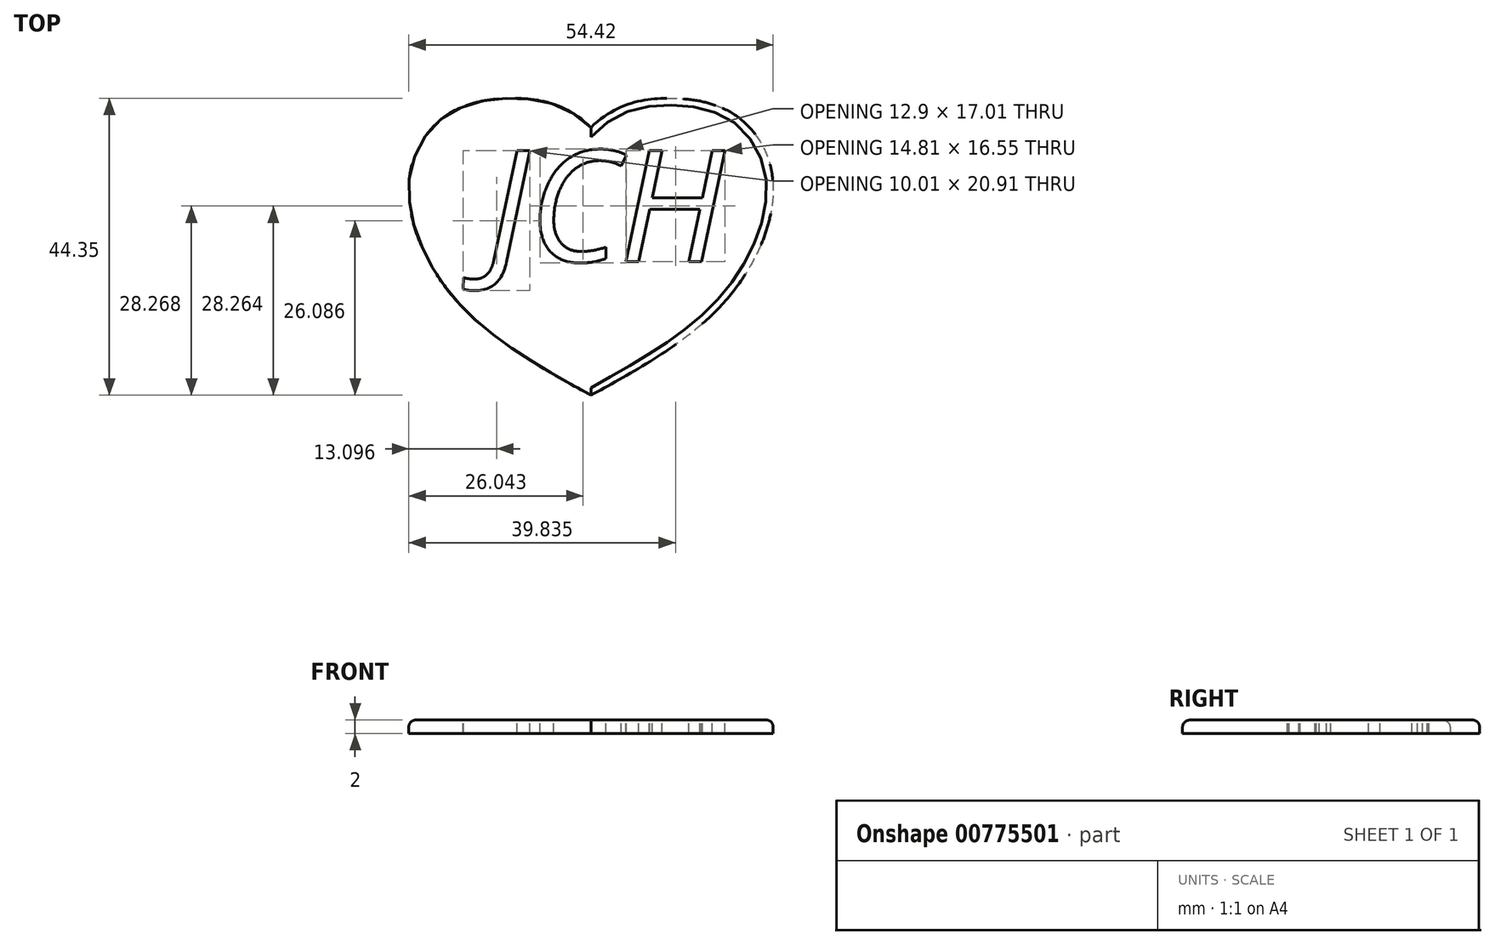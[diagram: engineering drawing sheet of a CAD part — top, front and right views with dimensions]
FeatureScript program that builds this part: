
annotation { "Feature Type Name" : "Feature", "Feature Type Description" : "" }
export const myFeature = defineFeature(function(context is Context, id is Id, definition is map)
    precondition{}
    {
        {
            var Q0;
            Q0=qCreatedBy(makeId("Top.planeOp"),FACE);
            var sketch = newSketch(context, id + "F0", { "sketchPlane" : qUnion([Q0])});
            skFitSpline(sketch, "E0", {"points": [v(0, 40) * mm, v(-12.4, 44.33) * mm, v(-18.67, 43.3) * mm, v(-23.19, 40.5) * mm, v(-26.76, 34.44) * mm, v(-26.76, 26.72) * mm, v(-24.3, 20.2) * mm, v(-19.7, 13.68) * mm, v(-11.24, 6.63) * mm, v(0, 0) * mm], "startDerivative": vector(-89.08, 87.77) * mm, "endDerivative": vector(67.58, -36.73) * mm});
            skLineSegment(sketch, "E1", {"start": v(0, 40) * mm, "end": v(0, 0) * mm});
            skSolve(sketch);
        }
        {
            var Q0;
            Q0=makeQuery(id+"F0.imprint","IMPRINT",FACE,{"disambiguationData":[TD([[makeQuery(id+"F0.imprint","IMPRINT",EDGE,{"derivedFrom":sQuery(id+"F0.wireOp",EDGE,"E0")}),1.0]])]});
            extrude(context, id + "F1", {"entities" : qUnion([Q0]), "depth" : 2 * mm, "offsetDistance" : 25 * mm});
        }
        {
            var Q0;
            Q0=makeQuery(id+"F1.opExtrude","SWEPT_BODY",BODY,{"disambiguationData":[OSD([sQuery(id+"F0.wireOp",EDGE,"E0"),sQuery(id+"F0.wireOp",EDGE,"E1")])]});
            var Q1;
            Q1=makeQuery(id+"F1.opExtrude","SWEPT_FACE",FACE,{"disambiguationData":[OSD([sQuery(id+"F0.wireOp",EDGE,"E1")])]});
            mirror(context, id + "F2", {"operationType" : NewBodyOperationType.ADD, "entities" : qUnion([Q0]), "mirrorPlane" : qUnion([Q1])});
        }
        {
            var Q0;
            {var subQ0=makeQuery(id+"F1.opExtrude","CAP_FACE",FACE,{"disambiguationData":[OSD([sQuery(id+"F0.wireOp",EDGE,"E0"),sQuery(id+"F0.wireOp",EDGE,"E1")])],"isStart":false});Q0=makeQuery(id+"F2.boolean.opBoolean","MERGE",FACE,{"derivedFrom":[subQ0,makeQuery(id+"F2.opPattern","COPY",FACE,{"derivedFrom":subQ0,"instanceName":"1"})]});}
            var sketch = newSketch(context, id + "F3", { "sketchPlane" : qUnion([Q0])});
            skText(sketch, "E2", { "text": " JCH", "fontName": "OpenSans-Italic.ttf"});
            const initialGuessF3  = {"E2": [-0.02153, 0.01999, 1, 0, 0.01669]};
            skSetInitialGuess(sketch, initialGuessF3);
            skSolve(sketch);
        }
        {
            var Q0;
            Q0=qSketchRegion(id+"F3",true);
            extrude(context, id + "F4", {"entities" : qUnion([Q0]), "operationType" : NewBodyOperationType.REMOVE, "oppositeDirection" : true, "depth" : 30 * mm, "offsetDistance" : 25 * mm});
        }
        {
            var Q0;
            Q0=makeQuery(id+"F2.opPattern","COPY",EDGE,{"derivedFrom":makeQuery(id+"F1.opExtrude","CAP_EDGE",EDGE,{"disambiguationData":[OSD([sQuery(id+"F0.wireOp",EDGE,"E0")])],"isStart":false}),"instanceName":"1"});
            var Q1;
            Q1=makeQuery(id+"F4.boolean.opBoolean","COPY",EDGE,{"derivedFrom":makeQuery(id+"F4.opExtrude","CAP_EDGE",EDGE,{"disambiguationData":[OSD([sQuery(id+"F3.wireOp",EDGE,"E2.sketch_text.stroke-37")])],"isStart":true})});
            var Q2;
            Q2=makeQuery(id+"F4.boolean.opBoolean","COPY",EDGE,{"derivedFrom":makeQuery(id+"F4.opExtrude","CAP_EDGE",EDGE,{"disambiguationData":[OSD([sQuery(id+"F3.wireOp",EDGE,"E2.sketch_text.stroke-3")])],"isStart":true})});
            var Q3;
            Q3=makeQuery(id+"F4.boolean.opBoolean","COPY",EDGE,{"derivedFrom":makeQuery(id+"F4.opExtrude","CAP_EDGE",EDGE,{"disambiguationData":[OSD([sQuery(id+"F3.wireOp",EDGE,"E2.sketch_text.stroke-54")])],"isStart":true})});
            var Q4;
            Q4=makeQuery(id+"F1.opExtrude","CAP_EDGE",EDGE,{"disambiguationData":[OSD([sQuery(id+"F0.wireOp",EDGE,"E0")])],"isStart":false});
            var Q5;
            Q5=makeQuery(id+"F4.boolean.opBoolean","COPY",EDGE,{"derivedFrom":makeQuery(id+"F4.opExtrude","CAP_EDGE",EDGE,{"disambiguationData":[OSD([sQuery(id+"F3.wireOp",EDGE,"E2.sketch_text.stroke-12")])],"isStart":true})});
            var Q6;
            Q6=makeQuery(id+"F4.boolean.opBoolean","COPY",EDGE,{"derivedFrom":makeQuery(id+"F4.opExtrude","CAP_EDGE",EDGE,{"disambiguationData":[OSD([sQuery(id+"F3.wireOp",EDGE,"E2.sketch_text.stroke-8")])],"isStart":true})});
            var Q7;
            Q7=makeQuery(id+"F4.boolean.opBoolean","COPY",EDGE,{"derivedFrom":makeQuery(id+"F4.opExtrude","CAP_EDGE",EDGE,{"disambiguationData":[OSD([sQuery(id+"F3.wireOp",EDGE,"E2.sketch_text.stroke-26")])],"isStart":true})});
            var Q8;
            Q8=makeQuery(id+"F4.boolean.opBoolean","COPY",EDGE,{"derivedFrom":makeQuery(id+"F4.opExtrude","CAP_EDGE",EDGE,{"disambiguationData":[OSD([sQuery(id+"F3.wireOp",EDGE,"E2.sketch_text.stroke-60")])],"isStart":true})});
            var Q9;
            Q9=makeQuery(id+"F4.boolean.opBoolean","COPY",EDGE,{"derivedFrom":makeQuery(id+"F4.opExtrude","CAP_EDGE",EDGE,{"disambiguationData":[OSD([sQuery(id+"F3.wireOp",EDGE,"E2.sketch_text.stroke-32")])],"isStart":true})});
            var Q10;
            Q10=makeQuery(id+"F4.boolean.opBoolean","COPY",EDGE,{"derivedFrom":makeQuery(id+"F4.opExtrude","CAP_EDGE",EDGE,{"disambiguationData":[OSD([sQuery(id+"F3.wireOp",EDGE,"E2.sketch_text.stroke-51")])],"isStart":true})});
            var Q11;
            Q11=makeQuery(id+"F4.boolean.opBoolean","COPY",EDGE,{"derivedFrom":makeQuery(id+"F4.opExtrude","CAP_EDGE",EDGE,{"disambiguationData":[OSD([sQuery(id+"F3.wireOp",EDGE,"E2.sketch_text.stroke-20")])],"isStart":true})});
            var Q12;
            Q12=makeQuery(id+"F4.boolean.opBoolean","COPY",EDGE,{"derivedFrom":makeQuery(id+"F4.opExtrude","CAP_EDGE",EDGE,{"disambiguationData":[OSD([sQuery(id+"F3.wireOp",EDGE,"E2.sketch_text.stroke-25")])],"isStart":true})});
            var Q13;
            Q13=makeQuery(id+"F4.boolean.opBoolean","COPY",EDGE,{"derivedFrom":makeQuery(id+"F4.opExtrude","CAP_EDGE",EDGE,{"disambiguationData":[OSD([sQuery(id+"F3.wireOp",EDGE,"E2.sketch_text.stroke-46")])],"isStart":true})});
            var Q14;
            Q14=makeQuery(id+"F4.boolean.opBoolean","COPY",EDGE,{"derivedFrom":makeQuery(id+"F4.opExtrude","CAP_EDGE",EDGE,{"disambiguationData":[OSD([sQuery(id+"F3.wireOp",EDGE,"E2.sketch_text.stroke-62")])],"isStart":true})});
            var Q15;
            Q15=makeQuery(id+"F4.boolean.opBoolean","COPY",EDGE,{"derivedFrom":makeQuery(id+"F4.opExtrude","CAP_EDGE",EDGE,{"disambiguationData":[OSD([sQuery(id+"F3.wireOp",EDGE,"E2.sketch_text.stroke-0")])],"isStart":true})});
            var Q16;
            Q16=makeQuery(id+"F4.boolean.opBoolean","COPY",EDGE,{"derivedFrom":makeQuery(id+"F4.opExtrude","CAP_EDGE",EDGE,{"disambiguationData":[OSD([sQuery(id+"F3.wireOp",EDGE,"E2.sketch_text.stroke-52")])],"isStart":true})});
            var Q17;
            Q17=makeQuery(id+"F4.boolean.opBoolean","COPY",EDGE,{"derivedFrom":makeQuery(id+"F4.opExtrude","CAP_EDGE",EDGE,{"disambiguationData":[OSD([sQuery(id+"F3.wireOp",EDGE,"E2.sketch_text.stroke-28")])],"isStart":true})});
            var Q18;
            Q18=makeQuery(id+"F4.boolean.opBoolean","COPY",EDGE,{"derivedFrom":makeQuery(id+"F4.opExtrude","CAP_EDGE",EDGE,{"disambiguationData":[OSD([sQuery(id+"F3.wireOp",EDGE,"E2.sketch_text.stroke-2")])],"isStart":true})});
            var Q19;
            Q19=makeQuery(id+"F4.boolean.opBoolean","COPY",EDGE,{"derivedFrom":makeQuery(id+"F4.opExtrude","CAP_EDGE",EDGE,{"disambiguationData":[OSD([sQuery(id+"F3.wireOp",EDGE,"E2.sketch_text.stroke-15")])],"isStart":true})});
            var Q20;
            Q20=makeQuery(id+"F4.boolean.opBoolean","COPY",EDGE,{"derivedFrom":makeQuery(id+"F4.opExtrude","CAP_EDGE",EDGE,{"disambiguationData":[OSD([sQuery(id+"F3.wireOp",EDGE,"E2.sketch_text.stroke-43")])],"isStart":true})});
            var Q21;
            Q21=makeQuery(id+"F4.boolean.opBoolean","COPY",EDGE,{"derivedFrom":makeQuery(id+"F4.opExtrude","CAP_EDGE",EDGE,{"disambiguationData":[OSD([sQuery(id+"F3.wireOp",EDGE,"E2.sketch_text.stroke-55")])],"isStart":true})});
            var Q22;
            Q22=makeQuery(id+"F4.boolean.opBoolean","COPY",EDGE,{"derivedFrom":makeQuery(id+"F4.opExtrude","CAP_EDGE",EDGE,{"disambiguationData":[OSD([sQuery(id+"F3.wireOp",EDGE,"E2.sketch_text.stroke-59")])],"isStart":true})});
            var Q23;
            Q23=makeQuery(id+"F4.boolean.opBoolean","COPY",EDGE,{"derivedFrom":makeQuery(id+"F4.opExtrude","CAP_EDGE",EDGE,{"disambiguationData":[OSD([sQuery(id+"F3.wireOp",EDGE,"E2.sketch_text.stroke-47")])],"isStart":true})});
            var Q24;
            Q24=makeQuery(id+"F4.boolean.opBoolean","COPY",EDGE,{"derivedFrom":makeQuery(id+"F4.opExtrude","CAP_EDGE",EDGE,{"disambiguationData":[OSD([sQuery(id+"F3.wireOp",EDGE,"E2.sketch_text.stroke-5")])],"isStart":true})});
            var Q25;
            Q25=makeQuery(id+"F4.boolean.opBoolean","COPY",EDGE,{"derivedFrom":makeQuery(id+"F4.opExtrude","CAP_EDGE",EDGE,{"disambiguationData":[OSD([sQuery(id+"F3.wireOp",EDGE,"E2.sketch_text.stroke-45")])],"isStart":true})});
            var Q26;
            Q26=makeQuery(id+"F4.boolean.opBoolean","COPY",EDGE,{"derivedFrom":makeQuery(id+"F4.opExtrude","CAP_EDGE",EDGE,{"disambiguationData":[OSD([sQuery(id+"F3.wireOp",EDGE,"E2.sketch_text.stroke-44")])],"isStart":true})});
            var Q27;
            Q27=makeQuery(id+"F4.boolean.opBoolean","COPY",EDGE,{"derivedFrom":makeQuery(id+"F4.opExtrude","CAP_EDGE",EDGE,{"disambiguationData":[OSD([sQuery(id+"F3.wireOp",EDGE,"E2.sketch_text.stroke-4")])],"isStart":true})});
            var Q28;
            Q28=makeQuery(id+"F4.boolean.opBoolean","COPY",EDGE,{"derivedFrom":makeQuery(id+"F4.opExtrude","CAP_EDGE",EDGE,{"disambiguationData":[OSD([sQuery(id+"F3.wireOp",EDGE,"E2.sketch_text.stroke-42")])],"isStart":true})});
            var Q29;
            Q29=makeQuery(id+"F4.boolean.opBoolean","COPY",EDGE,{"derivedFrom":makeQuery(id+"F4.opExtrude","CAP_EDGE",EDGE,{"disambiguationData":[OSD([sQuery(id+"F3.wireOp",EDGE,"E2.sketch_text.stroke-57")])],"isStart":true})});
            var Q30;
            Q30=makeQuery(id+"F4.boolean.opBoolean","COPY",EDGE,{"derivedFrom":makeQuery(id+"F4.opExtrude","CAP_EDGE",EDGE,{"disambiguationData":[OSD([sQuery(id+"F3.wireOp",EDGE,"E2.sketch_text.stroke-22")])],"isStart":true})});
            var Q31;
            Q31=makeQuery(id+"F4.boolean.opBoolean","COPY",EDGE,{"derivedFrom":makeQuery(id+"F4.opExtrude","CAP_EDGE",EDGE,{"disambiguationData":[OSD([sQuery(id+"F3.wireOp",EDGE,"E2.sketch_text.stroke-18")])],"isStart":true})});
            var Q32;
            Q32=makeQuery(id+"F4.boolean.opBoolean","COPY",EDGE,{"derivedFrom":makeQuery(id+"F4.opExtrude","CAP_EDGE",EDGE,{"disambiguationData":[OSD([sQuery(id+"F3.wireOp",EDGE,"E2.sketch_text.stroke-1")])],"isStart":true})});
            var Q33;
            Q33=makeQuery(id+"F4.boolean.opBoolean","COPY",EDGE,{"derivedFrom":makeQuery(id+"F4.opExtrude","CAP_EDGE",EDGE,{"disambiguationData":[OSD([sQuery(id+"F3.wireOp",EDGE,"E2.sketch_text.stroke-7")])],"isStart":true})});
            var Q34;
            Q34=makeQuery(id+"F4.boolean.opBoolean","COPY",EDGE,{"derivedFrom":makeQuery(id+"F4.opExtrude","CAP_EDGE",EDGE,{"disambiguationData":[OSD([sQuery(id+"F3.wireOp",EDGE,"E2.sketch_text.stroke-9")])],"isStart":true})});
            var Q35;
            Q35=makeQuery(id+"F4.boolean.opBoolean","COPY",EDGE,{"derivedFrom":makeQuery(id+"F4.opExtrude","CAP_EDGE",EDGE,{"disambiguationData":[OSD([sQuery(id+"F3.wireOp",EDGE,"E2.sketch_text.stroke-11")])],"isStart":true})});
            var Q36;
            Q36=makeQuery(id+"F4.boolean.opBoolean","COPY",EDGE,{"derivedFrom":makeQuery(id+"F4.opExtrude","CAP_EDGE",EDGE,{"disambiguationData":[OSD([sQuery(id+"F3.wireOp",EDGE,"E2.sketch_text.stroke-6")])],"isStart":true})});
            var Q37;
            Q37=makeQuery(id+"F4.boolean.opBoolean","COPY",EDGE,{"derivedFrom":makeQuery(id+"F4.opExtrude","CAP_EDGE",EDGE,{"disambiguationData":[OSD([sQuery(id+"F3.wireOp",EDGE,"E2.sketch_text.stroke-53")])],"isStart":true})});
            var Q38;
            Q38=makeQuery(id+"F4.boolean.opBoolean","COPY",EDGE,{"derivedFrom":makeQuery(id+"F4.opExtrude","CAP_EDGE",EDGE,{"disambiguationData":[OSD([sQuery(id+"F3.wireOp",EDGE,"E2.sketch_text.stroke-38")])],"isStart":true})});
            var Q39;
            Q39=makeQuery(id+"F4.boolean.opBoolean","COPY",EDGE,{"derivedFrom":makeQuery(id+"F4.opExtrude","CAP_EDGE",EDGE,{"disambiguationData":[OSD([sQuery(id+"F3.wireOp",EDGE,"E2.sketch_text.stroke-24")])],"isStart":true})});
            var Q40;
            Q40=makeQuery(id+"F4.boolean.opBoolean","COPY",EDGE,{"derivedFrom":makeQuery(id+"F4.opExtrude","CAP_EDGE",EDGE,{"disambiguationData":[OSD([sQuery(id+"F3.wireOp",EDGE,"E2.sketch_text.stroke-58")])],"isStart":true})});
            var Q41;
            Q41=makeQuery(id+"F4.boolean.opBoolean","COPY",EDGE,{"derivedFrom":makeQuery(id+"F4.opExtrude","CAP_EDGE",EDGE,{"disambiguationData":[OSD([sQuery(id+"F3.wireOp",EDGE,"E2.sketch_text.stroke-61")])],"isStart":true})});
            var Q42;
            Q42=makeQuery(id+"F4.boolean.opBoolean","COPY",EDGE,{"derivedFrom":makeQuery(id+"F4.opExtrude","CAP_EDGE",EDGE,{"disambiguationData":[OSD([sQuery(id+"F3.wireOp",EDGE,"E2.sketch_text.stroke-41")])],"isStart":true})});
            var Q43;
            Q43=makeQuery(id+"F4.boolean.opBoolean","COPY",EDGE,{"derivedFrom":makeQuery(id+"F4.opExtrude","CAP_EDGE",EDGE,{"disambiguationData":[OSD([sQuery(id+"F3.wireOp",EDGE,"E2.sketch_text.stroke-14")])],"isStart":true})});
            var Q44;
            Q44=makeQuery(id+"F4.boolean.opBoolean","COPY",EDGE,{"derivedFrom":makeQuery(id+"F4.opExtrude","CAP_EDGE",EDGE,{"disambiguationData":[OSD([sQuery(id+"F3.wireOp",EDGE,"E2.sketch_text.stroke-36")])],"isStart":true})});
            var Q45;
            Q45=makeQuery(id+"F4.boolean.opBoolean","COPY",EDGE,{"derivedFrom":makeQuery(id+"F4.opExtrude","CAP_EDGE",EDGE,{"disambiguationData":[OSD([sQuery(id+"F3.wireOp",EDGE,"E2.sketch_text.stroke-50")])],"isStart":true})});
            var Q46;
            Q46=makeQuery(id+"F4.boolean.opBoolean","COPY",EDGE,{"derivedFrom":makeQuery(id+"F4.opExtrude","CAP_EDGE",EDGE,{"disambiguationData":[OSD([sQuery(id+"F3.wireOp",EDGE,"E2.sketch_text.stroke-27")])],"isStart":true})});
            var Q47;
            Q47=makeQuery(id+"F4.boolean.opBoolean","COPY",EDGE,{"derivedFrom":makeQuery(id+"F4.opExtrude","CAP_EDGE",EDGE,{"disambiguationData":[OSD([sQuery(id+"F3.wireOp",EDGE,"E2.sketch_text.stroke-48")])],"isStart":true})});
            var Q48;
            Q48=makeQuery(id+"F4.boolean.opBoolean","COPY",EDGE,{"derivedFrom":makeQuery(id+"F4.opExtrude","CAP_EDGE",EDGE,{"disambiguationData":[OSD([sQuery(id+"F3.wireOp",EDGE,"E2.sketch_text.stroke-13")])],"isStart":true})});
            var Q49;
            Q49=makeQuery(id+"F4.boolean.opBoolean","COPY",EDGE,{"derivedFrom":makeQuery(id+"F4.opExtrude","CAP_EDGE",EDGE,{"disambiguationData":[OSD([sQuery(id+"F3.wireOp",EDGE,"E2.sketch_text.stroke-56")])],"isStart":true})});
            var Q50;
            Q50=makeQuery(id+"F4.boolean.opBoolean","COPY",EDGE,{"derivedFrom":makeQuery(id+"F4.opExtrude","CAP_EDGE",EDGE,{"disambiguationData":[OSD([sQuery(id+"F3.wireOp",EDGE,"E2.sketch_text.stroke-35")])],"isStart":true})});
            var Q51;
            Q51=makeQuery(id+"F4.boolean.opBoolean","COPY",EDGE,{"derivedFrom":makeQuery(id+"F4.opExtrude","CAP_EDGE",EDGE,{"disambiguationData":[OSD([sQuery(id+"F3.wireOp",EDGE,"E2.sketch_text.stroke-29")])],"isStart":true})});
            var Q52;
            Q52=makeQuery(id+"F4.boolean.opBoolean","COPY",EDGE,{"derivedFrom":makeQuery(id+"F4.opExtrude","CAP_EDGE",EDGE,{"disambiguationData":[OSD([sQuery(id+"F3.wireOp",EDGE,"E2.sketch_text.stroke-21")])],"isStart":true})});
            var Q53;
            Q53=makeQuery(id+"F4.boolean.opBoolean","COPY",EDGE,{"derivedFrom":makeQuery(id+"F4.opExtrude","CAP_EDGE",EDGE,{"disambiguationData":[OSD([sQuery(id+"F3.wireOp",EDGE,"E2.sketch_text.stroke-49")])],"isStart":true})});
            var Q54;
            Q54=makeQuery(id+"F4.boolean.opBoolean","COPY",EDGE,{"derivedFrom":makeQuery(id+"F4.opExtrude","CAP_EDGE",EDGE,{"disambiguationData":[OSD([sQuery(id+"F3.wireOp",EDGE,"E2.sketch_text.stroke-30")])],"isStart":true})});
            var Q55;
            Q55=makeQuery(id+"F4.boolean.opBoolean","COPY",EDGE,{"derivedFrom":makeQuery(id+"F4.opExtrude","CAP_EDGE",EDGE,{"disambiguationData":[OSD([sQuery(id+"F3.wireOp",EDGE,"E2.sketch_text.stroke-34")])],"isStart":true})});
            var Q56;
            Q56=makeQuery(id+"F4.boolean.opBoolean","COPY",EDGE,{"derivedFrom":makeQuery(id+"F4.opExtrude","CAP_EDGE",EDGE,{"disambiguationData":[OSD([sQuery(id+"F3.wireOp",EDGE,"E2.sketch_text.stroke-31")])],"isStart":true})});
            var Q57;
            Q57=makeQuery(id+"F4.boolean.opBoolean","COPY",EDGE,{"derivedFrom":makeQuery(id+"F4.opExtrude","CAP_EDGE",EDGE,{"disambiguationData":[OSD([sQuery(id+"F3.wireOp",EDGE,"E2.sketch_text.stroke-10")])],"isStart":true})});
            var Q58;
            Q58=makeQuery(id+"F4.boolean.opBoolean","COPY",EDGE,{"derivedFrom":makeQuery(id+"F4.opExtrude","CAP_EDGE",EDGE,{"disambiguationData":[OSD([sQuery(id+"F3.wireOp",EDGE,"E2.sketch_text.stroke-16")])],"isStart":true})});
            var Q59;
            Q59=makeQuery(id+"F4.boolean.opBoolean","COPY",EDGE,{"derivedFrom":makeQuery(id+"F4.opExtrude","CAP_EDGE",EDGE,{"disambiguationData":[OSD([sQuery(id+"F3.wireOp",EDGE,"E2.sketch_text.stroke-19")])],"isStart":true})});
            var Q60;
            Q60=makeQuery(id+"F4.boolean.opBoolean","COPY",EDGE,{"derivedFrom":makeQuery(id+"F4.opExtrude","CAP_EDGE",EDGE,{"disambiguationData":[OSD([sQuery(id+"F3.wireOp",EDGE,"E2.sketch_text.stroke-17")])],"isStart":true})});
            var Q61;
            Q61=makeQuery(id+"F4.boolean.opBoolean","COPY",EDGE,{"derivedFrom":makeQuery(id+"F4.opExtrude","CAP_EDGE",EDGE,{"disambiguationData":[OSD([sQuery(id+"F3.wireOp",EDGE,"E2.sketch_text.stroke-33")])],"isStart":true})});
            var Q62;
            Q62=makeQuery(id+"F4.boolean.opBoolean","COPY",EDGE,{"derivedFrom":makeQuery(id+"F4.opExtrude","CAP_EDGE",EDGE,{"disambiguationData":[OSD([sQuery(id+"F3.wireOp",EDGE,"E2.sketch_text.stroke-39")])],"isStart":true})});
            var Q63;
            Q63=makeQuery(id+"F4.boolean.opBoolean","COPY",EDGE,{"derivedFrom":makeQuery(id+"F4.opExtrude","CAP_EDGE",EDGE,{"disambiguationData":[OSD([sQuery(id+"F3.wireOp",EDGE,"E2.sketch_text.stroke-23")])],"isStart":true})});
            var Q64;
            Q64=makeQuery(id+"F4.boolean.opBoolean","COPY",EDGE,{"derivedFrom":makeQuery(id+"F4.opExtrude","CAP_EDGE",EDGE,{"disambiguationData":[OSD([sQuery(id+"F3.wireOp",EDGE,"E2.sketch_text.stroke-40")])],"isStart":true})});
            fillet(context, id + "F5", {"entities" : qUnion([Q0, Q1, Q2, Q3, Q4, Q5, Q6, Q7, Q8, Q9, Q10, Q11, Q12, Q13, Q14, Q15, Q16, Q17, Q18, Q19, Q20, Q21, Q22, Q23, Q24, Q25, Q26, Q27, Q28, Q29, Q30, Q31, Q32, Q33, Q34, Q35, Q36, Q37, Q38, Q39, Q40, Q41, Q42, Q43, Q44, Q45, Q46, Q47, Q48, Q49, Q50, Q51, Q52, Q53, Q54, Q55, Q56, Q57, Q58, Q59, Q60, Q61, Q62, Q63, Q64]), "radius" : 1 * mm, "tangentPropagation" : true, "allowEdgeOverflow" : false});
        }
    });
